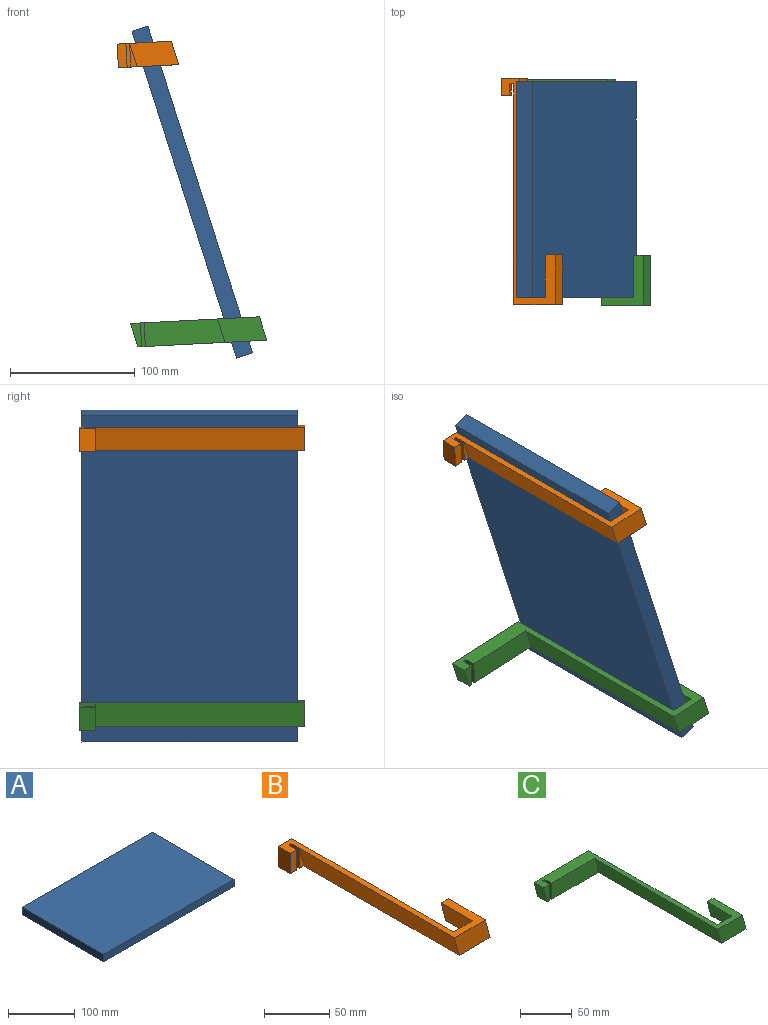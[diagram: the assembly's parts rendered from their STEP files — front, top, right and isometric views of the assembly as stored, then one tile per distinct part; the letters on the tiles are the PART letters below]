
ASSEMBLY  parts=3 mates=5
PART A: 6 faces, bbox 275x173x13.5 mm
  f0: plane 173x13.5mm, normal (-1,0,0), area 2335.5mm2, adj f1,f3,f4,f5
  f1: plane 275x13.5mm, normal (0,-1,0), area 3712.5mm2, adj f0,f2,f4,f5
  f2: plane 173x13.5mm, normal (1,0,0), area 2335.5mm2, adj f1,f3,f4,f5
  f3: plane 275x13.5mm, normal (0,1,0), area 3712.5mm2, adj f0,f2,f4,f5
  f4: plane 275x173mm, normal (0,0,1), area 47575mm2, adj f0,f1,f2,f3
  f5: plane 275x173mm, normal (0,0,-1), area 47575mm2, adj f0,f1,f2,f3
PART B: 16 faces, bbox 48.5x181x19 mm
  f0: plane 19x7mm, normal (0,-1,0), area 133mm2, adj f1,f2,f11,f13
  f1: plane 181x48.5mm, normal (0,0,-1), area 1516mm2, adj f0,f3,f4,f5,f6,f7,f8,f9
  f2: plane 181x43.5mm, normal (0,0,1), area 1451mm2, adj f0,f3,f4,f5,f6,f7,f8,f9
  f3: plane 168x19mm, normal (-0.97,0,-0.25), area 3300.7mm2, adj f1,f2,f4,f12
  f4: plane 38.5x19mm, normal (0,-1,0), area 636.5mm2, adj f1,f2,f3,f5
  f5: plane 40x19mm, normal (0.97,0,0.25), area 785.9mm2, adj f1,f2,f4,f6
  f6: plane 19x13mm, normal (0,1,0), area 152mm2, adj f1,f2,f5,f7
  f7: plane 34x19mm, normal (-0.97,0,-0.25), area 668mm2, adj f1,f2,f6,f8
  f8: plane 25.5x19mm, normal (0,1,0), area 389.5mm2, adj f1,f2,f7,f9
  f9: plane 175x19mm, normal (0.97,0,0.25), area 3438.2mm2, adj f1,f2,f8,f10
  f10: plane 20x19mm, normal (0,1,0), area 332.5mm2, adj f1,f2,f9,f11
  f11: plane 19x13mm, normal (-1,0,0), area 247mm2, adj f0,f1,f2,f10
  f12: plane 19x5mm, normal (0,-1,0), area 47.5mm2, adj f1,f3,f14
  f13: plane 19x9mm, normal (1,0,0), area 171mm2, adj f0,f1,f2,f15
  f14: plane 19x9mm, normal (-1,0,0), area 171mm2, adj f1,f2,f12,f15
  f15: plane 19x3mm, normal (0,-1,0), area 57mm2, adj f1,f2,f13,f14
PART C: 16 faces, bbox 108.5x181x19 mm
  f0: plane 19x8mm, normal (0,-1,0), area 104.5mm2, adj f1,f2,f11,f13
  f1: plane 181x103.5mm, normal (0,0,-1), area 2231mm2, adj f0,f3,f4,f5,f6,f7,f8,f9
  f2: plane 181x103.5mm, normal (0,0,1), area 2231mm2, adj f0,f3,f4,f5,f6,f7,f8,f9
  f3: plane 168x19mm, normal (-0.97,0,-0.25), area 3300.7mm2, adj f1,f2,f4,f12
  f4: plane 38.5x19mm, normal (0,-1,0), area 636.5mm2, adj f1,f2,f3,f5
  f5: plane 40x19mm, normal (0.97,0,0.25), area 785.9mm2, adj f1,f2,f4,f6
  f6: plane 19x13mm, normal (0,1,0), area 152mm2, adj f1,f2,f5,f7
  f7: plane 34x19mm, normal (-0.97,0,-0.25), area 668mm2, adj f1,f2,f6,f8
  f8: plane 25.5x19mm, normal (0,1,0), area 389.5mm2, adj f1,f2,f7,f9
  f9: plane 175x19mm, normal (0.97,0,0.25), area 3438.2mm2, adj f1,f2,f8,f10
  f10: plane 80x19mm, normal (0,1,0), area 1425mm2, adj f1,f2,f9,f11
  f11: plane 19x13mm, normal (-0.97,0,-0.25), area 255.4mm2, adj f0,f1,f2,f10
  f12: plane 64x19mm, normal (0,-1,0), area 1168.5mm2, adj f1,f2,f3,f14
  f13: plane 19x9mm, normal (1,0,0), area 171mm2, adj f0,f1,f2,f15
  f14: plane 19x9mm, normal (-1,0,0), area 171mm2, adj f1,f2,f12,f15
  f15: plane 19x3mm, normal (0,-1,0), area 57mm2, adj f1,f2,f13,f14
PLACE A rot(axis=(0,1,0),72.3deg) t=(-310.81,-134.82,113.03)mm
PLACE B rot(axis=(0,-1,0),3deg) t=(-328.36,-73.68,218.45)mm
PLACE C rot(axis=(0,-1,0),3deg) t=(-282.03,-94.95,-3.64)mm
MATE planar B.f9 <-> A.f5  axis (0.95,0,0.3) through (-347.21,-118.95,226.99)mm
MATE planar B.f10 <-> C.f10  axis (0,1,0) through (-355.87,-31.45,226.09)mm
MATE planar C.f8 <-> A.f1  axis (0,1,0) through (-266.44,-206.45,6.68)mm
MATE planar C.f13 <-> B.f13  axis (1,0,0.05) through (-346.08,-39.95,2.55)mm
MATE planar C.f9 <-> A.f5  axis (0.95,0,0.3) through (-276.68,-118.95,6.15)mm
